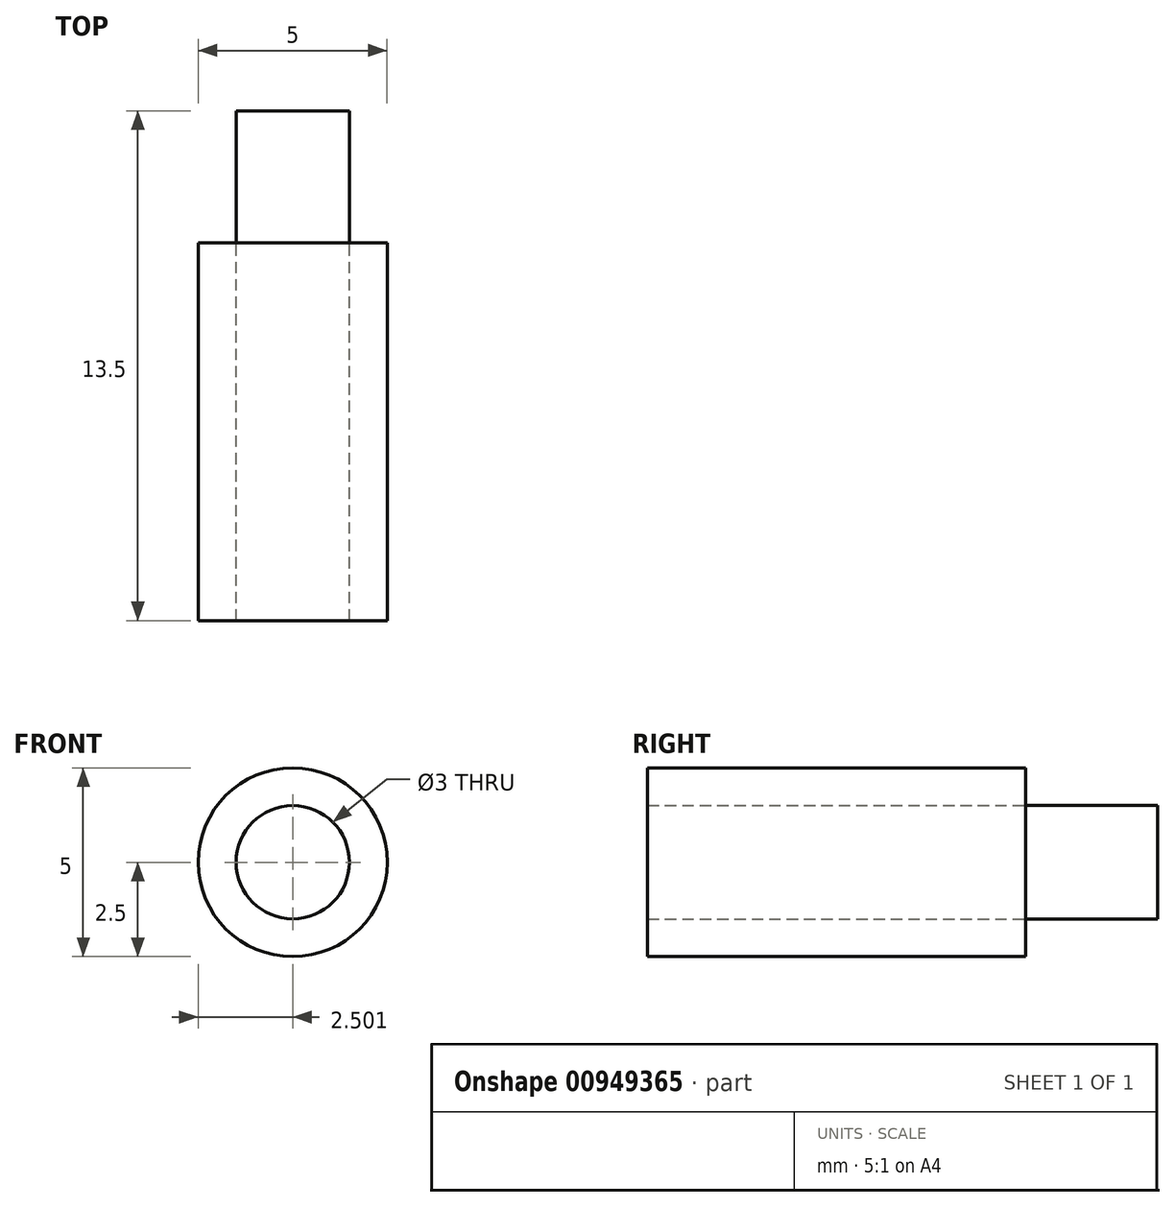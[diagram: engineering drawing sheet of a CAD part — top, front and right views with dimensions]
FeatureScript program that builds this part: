
annotation { "Feature Type Name" : "Feature", "Feature Type Description" : "" }
export const myFeature = defineFeature(function(context is Context, id is Id, definition is map)
    precondition{}
    {
        {
            var Q0;
            Q0=qCreatedBy(makeId("Front.planeOp"),FACE);
            var sketch = newSketch(context, id + "F0", { "sketchPlane" : qUnion([Q0])});
            skLineSegment(sketch, "E0", {"start": v(59.15, 0) * mm, "end": v(-48, 0) * mm, "construction": true});
            skLineSegment(sketch, "E1", {"start": v(0.57, -12.5) * mm, "end": v(0.57, 12.5) * mm, "construction": true});
            skPoint(sketch, "E2", {"position": v(-3.43, 0) * mm});
            skCircle(sketch, "E3", {"center": v(-3.43, 0) * mm, "radius": 2.5 * mm});
            skCircle(sketch, "E4.MirrorC", {"center": v(4.57, 0) * mm, "radius": 2.5 * mm});
            skCircle(sketch, "E5", {"center": v(-3.43, 0) * mm, "radius": 1.5 * mm});
            skCircle(sketch, "E6.MirrorC", {"center": v(4.57, 0) * mm, "radius": 1.5 * mm});
            skSolve(sketch);
        }
        {
            var Q0;
            Q0=makeQuery(id+"F0.imprint","IMPRINT",FACE,{"disambiguationData":[TD([[makeQuery(id+"F0.imprint","IMPRINT",EDGE,{"derivedFrom":sQuery(id+"F0.wireOp",EDGE,"E3")}),1.0]])]});
            var Q1;
            Q1=makeQuery(id+"F0.imprint","IMPRINT",FACE,{"disambiguationData":[TD([[makeQuery(id+"F0.imprint","IMPRINT",EDGE,{"derivedFrom":sQuery(id+"F0.wireOp",EDGE,"E4.MirrorC")}),-1.0]])]});
            extrude(context, id + "F1", {"entities" : qUnion([Q0, Q1]), "depth" : 10 * mm, "offsetDistance" : 25 * mm});
        }
        {
            var Q0;
            Q0=makeQuery(id+"F1.opExtrude","CAP_FACE",FACE,{"disambiguationData":[OSD([sQuery(id+"F0.wireOp",EDGE,"E3"),sQuery(id+"F0.wireOp",EDGE,"E5")])],"isStart":true});
            var sketch = newSketch(context, id + "F2", { "sketchPlane" : qUnion([Q0])});
            skSolve(sketch);
        }
        {
            var Q0;
            Q0=makeQuery(id+"F1.opExtrude","CAP_FACE",FACE,{"disambiguationData":[OSD([sQuery(id+"F0.wireOp",EDGE,"E4.MirrorC"),sQuery(id+"F0.wireOp",EDGE,"E6.MirrorC")])],"isStart":true});
            var sketch = newSketch(context, id + "F3", { "sketchPlane" : qUnion([Q0])});
            skSolve(sketch);
        }
        {
            var Q0;
            Q0=makeQuery(id+"F3.imprint","IMPRINT",FACE,{"disambiguationData":[TD([[makeQuery(id+"F3.imprint","IMPRINT",EDGE,{"derivedFrom":makeQuery(id+"F1.opExtrude","CAP_EDGE",EDGE,{"disambiguationData":[OSD([sQuery(id+"F0.wireOp",EDGE,"E6.MirrorC")])],"isStart":true})}),1.0]])]});
            var Q1;
            Q1=makeQuery(id+"F2.imprint","IMPRINT",FACE,{"disambiguationData":[TD([[makeQuery(id+"F2.imprint","IMPRINT",EDGE,{"derivedFrom":makeQuery(id+"F1.opExtrude","CAP_EDGE",EDGE,{"disambiguationData":[OSD([sQuery(id+"F0.wireOp",EDGE,"E5")])],"isStart":true})}),-1.0]])]});
            extrude(context, id + "F4", {"entities" : qUnion([Q0, Q1]), "depth" : 3.5 * mm, "offsetDistance" : 25 * mm});
        }
    });
